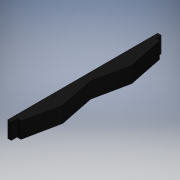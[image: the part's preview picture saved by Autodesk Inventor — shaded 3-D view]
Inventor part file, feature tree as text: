
AUTODESK INVENTOR PART (.ipt)
format: ipt  version: 2017 (Build 210142000, 142)  size: 119,296 bytes
history: native  units: in
note: dims shown in document units (in); Inventor stores cm internally (conversion verified against a paired STEP export)
features: extrude x3, sketch x3
ambient origin geometry x8: Origin, YZ Plane, XZ Plane, XY Plane, X Axis, Y Axis, Z Axis, Center Point
bodies: Solid1 (feature_tree)
feature tree (6):
  extrude  "Extrusion1"  Depth=0.134in
  sketch  "Sketch2"  dims[d2=0.134in d3=0.6115in]
  extrude  "Extrusion2"  Depth=0.134in
  extrude  "Extrusion3"  Depth=0.101in
  sketch  "Sketch1"  dims[d0=2.436in d1=0.134in]
  sketch  "Sketch3"  dims[d4=1.223in d5=0.6115in d6=0.125in d7=0.125in d8=0.2875in d9=0.0in d10=0.065in d11=0.065in d12=0.101in d13=0.0in d14=0.101in d15=0.0in]
